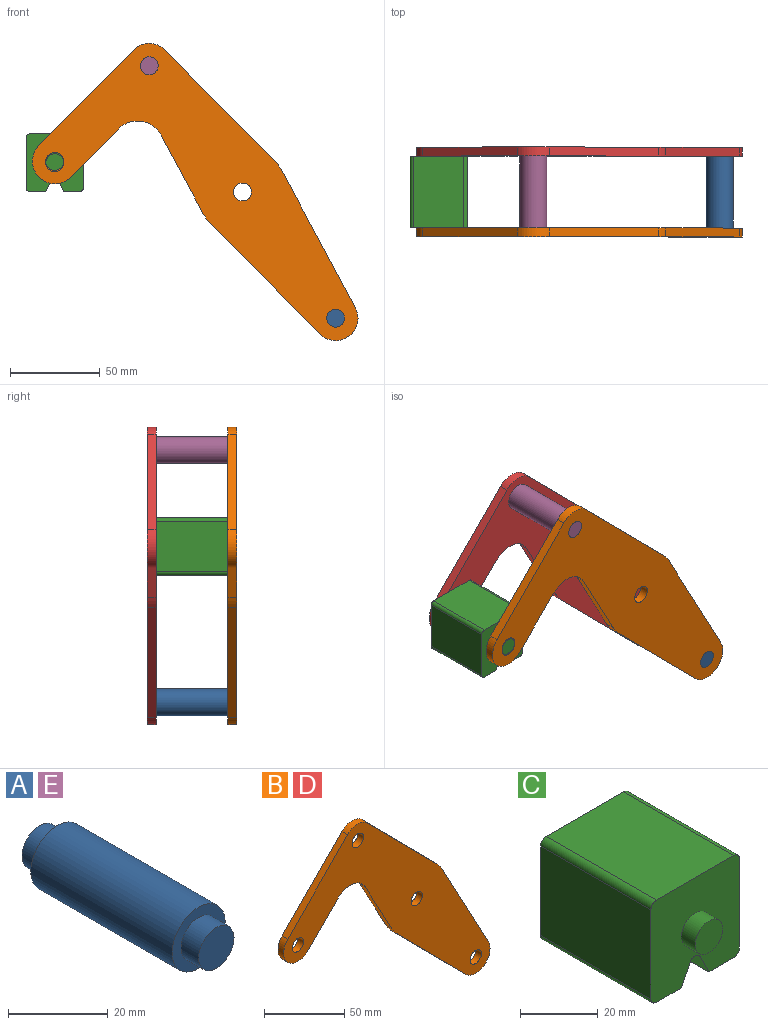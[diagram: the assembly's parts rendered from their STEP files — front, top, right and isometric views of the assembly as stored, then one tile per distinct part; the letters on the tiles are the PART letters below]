
ASSEMBLY  parts=5 mates=3
PART A: 7 faces, bbox 15x50x15 mm
  f0: cylinder r=7.5mm len=40mm, axis (0,-1,0), area 1885mm2, adj f2,f5
  f1: cylinder r=5mm len=10mm, axis (0,1,0), area 157.1mm2, adj f2,f3
  f2: plane 15x15mm, normal (0,-1,0), area 98.2mm2, adj f0,f1
  f3: plane 10x10mm, normal (0,-1,0), area 78.5mm2, adj f1
  f4: cylinder r=5mm len=10mm, axis (0,-1,0), area 157.1mm2, adj f5,f6
  f5: plane 15x15mm, normal (0,1,0), area 98.2mm2, adj f0,f4
  f6: plane 10x10mm, normal (0,1,0), area 78.5mm2, adj f4
PART B: 18 faces, bbox 181.7x5x165.8 mm
  f0: plane 43.49x23.35mm, normal (-0.88,0,-0.47), area 246.8mm2, adj f1,f14,f16,f17
  f1: cylinder r=25mm len=5.75mm, axis (0,1,0), area 35.8mm2, adj f0,f2,f16,f17
  f2: plane 61.6x60.87mm, normal (-0.71,0,-0.7), area 433mm2, adj f1,f3,f16,f17
  f3: cylinder r=12.5mm len=21.39mm, axis (0,1,0), area 178.4mm2, adj f2,f4,f16,f17
  f4: plane 76.3x40.96mm, normal (0.88,0,0.47), area 433mm2, adj f3,f5,f16,f17
  f5: cylinder r=25mm len=5.75mm, axis (0,1,0), area 35.8mm2, adj f4,f6,f16,f17
  f6: plane 61.6x60.87mm, normal (0.71,0,0.7), area 433mm2, adj f5,f7,f16,f17
  f7: cylinder r=12.5mm len=17.78mm, axis (0,1,0), area 98.9mm2, adj f6,f8,f16,f17
  f8: plane 53.35x52.71mm, normal (-0.71,0,0.7), area 375mm2, adj f7,f9,f16,f17
  f9: cylinder r=12.5mm len=21.39mm, axis (0,1,0), area 196.3mm2, adj f8,f10,f16,f17
  f10: plane 26.86x26.54mm, normal (0.71,0,-0.7), area 188.8mm2, adj f9,f14,f16,f17
  f11: cylinder r=5mm len=10mm, axis (0,1,0), area 157.1mm2, adj f16,f17
  f12: cylinder r=5mm len=10mm, axis (0,1,0), area 157.1mm2, adj f16,f17
  f13: cylinder r=5mm len=10mm, axis (0,1,0), area 157.1mm2, adj f16,f17
  f14: cylinder r=15mm len=23.89mm, axis (0,1,0), area 140.2mm2, adj f0,f10,f16,f17
  f15: cylinder r=5mm len=10mm, axis (0,1,0), area 157.1mm2, adj f16,f17
  f16: plane 181.66x165.78mm, normal (0,-1,0), area 8710.1mm2, adj f0,f1,f2,f3,f4,f5,f6,f7
  f17: plane 181.66x165.78mm, normal (0,1,0), area 8710.1mm2, adj f0,f1,f2,f3,f4,f5,f6,f7
PART C: 18 faces, bbox 32.1x50x32.1 mm
  f0: plane 40x28.08mm, normal (1,0,0), area 1123.1mm2, adj f4,f10,f13,f14
  f1: plane 40x9.04mm, normal (0,0,-1), area 361.6mm2, adj f2,f4,f10,f14
  f2: plane 40x6.42mm, normal (-0.89,0,-0.45), area 287.2mm2, adj f1,f4,f10,f15
  f3: plane 40x6.42mm, normal (0.89,0,-0.45), area 287.2mm2, adj f4,f5,f10,f15
  f4: plane 32.08x32.08mm, normal (0,-1,0), area 900.6mm2, adj f0,f1,f2,f3,f5,f6,f7,f9
  f5: plane 40x9.04mm, normal (0,0,-1), area 361.6mm2, adj f3,f4,f10,f16
  f6: plane 40x28.08mm, normal (0,0,1), area 1123.1mm2, adj f4,f10,f13,f17
  f7: plane 40x28.08mm, normal (-1,0,0), area 1123.1mm2, adj f4,f10,f16,f17
  f8: plane 10x10mm, normal (0,-1,0), area 78.5mm2, adj f9
  f9: cylinder r=5mm len=10mm, axis (0,1,0), area 157.1mm2, adj f4,f8
  f10: plane 32.08x32.08mm, normal (0,1,0), area 900.6mm2, adj f0,f1,f2,f3,f5,f6,f7,f12
  f11: plane 10x10mm, normal (0,1,0), area 78.5mm2, adj f12
  f12: cylinder r=5mm len=10mm, axis (0,-1,0), area 157.1mm2, adj f10,f11
  f13: cylinder r=2mm len=40mm, axis (0,1,0), area 125.7mm2, adj f0,f4,f6,f10
  f14: cylinder r=2mm len=40mm, axis (0,-1,0), area 125.7mm2, adj f0,f1,f4,f10
  f15: cylinder r=2mm len=40mm, axis (0,1,0), area 177.1mm2, adj f2,f3,f4,f10
  f16: cylinder r=2mm len=40mm, axis (0,1,0), area 125.7mm2, adj f4,f5,f7,f10
  f17: cylinder r=2mm len=40mm, axis (0,-1,0), area 125.7mm2, adj f4,f6,f7,f10
PART D: same geometry as B
PART E: same geometry as A
PLACE A t=(103.95,-20,-140.78)mm
PLACE B t=(0,-20,0)mm fixed
PLACE C t=(0,-20,-0.67)mm
PLACE D t=(0,25,0)mm
PLACE E t=(0,-20,0)mm
MATE revolute B.f9 <-> C.f4  axis (0,1,0) through (-104.69,-20,17.04)mm
MATE fastened E.f0 <-> D.f7  axis (0,1,0) through (-51.98,20,70.39)mm
MATE fastened A.f0 <-> B.f3  axis (0,-1,0) through (51.98,-20,-70.39)mm
